# Revit family: KS ALU-PU 80 -s-, DS 50, M10-M12, Ø 88,9-168,3
name_source: partatom
category: HLS-Bauteile
revit_build: Autodesk Revit 2017 (Build: 20190507_1515(x64)
units: mm (PartAtom-declared; Revit-internal decimal feet)

## family parameters
Arbeitsebenenbasiert = Ja
Beim Laden mit Abzugskörper schneiden = Nein
Bemaßung runder Anschluss = Durchmesser verwenden
Gemeinsam genutzt = Ja
Immer vertikal = Nein
Raumberechnungspunkt = Nein
Teiletyp = Normal

## types (7) — shared parameters
Anschluss = M10/M12
Baustoffklasse = B2
DS = 50 mm  [stored 0.164042 ft]
DVS = 18 mm  [stored 0.0590551 ft]
Dichte Kern = 80 kg/m³
Dichte Mantel = 2.700 kg/m³
Dicke Mantel = 0,08 mm
Dämmkörper = ALU/PU
Dämmstärke = 50 mm  [stored 0.164042 ft]
Fabrikat = MEFA
Firma = MEFA Befestigungs- und Montagesysteme GmbH
HGA = 22 mm  [stored 0.0721785 ft]
Kurztext1 = Kälteschelle RG80s ALU/PU
Material = Stahl
Material Mantel = Alufolie
Materialname = S235
Mengeneinheit = St
Oberflaeche = galvanisch verzinkt
Rohrschellentyp = Maxima PSM
Vorgabe-Ansicht = 1219 mm
Wasserdampfdiffusionswiderstand = 18750 µ
Wärmeleitfähigkeit = 0.025 W/mK
max. Temperaturbeständigkeit = 120 °C
mittl. Nenndruckfestigkeit Kern = 0,5 N/mm²
stat. Belastung Kern = 0,1 N/mm²
vpe = 1 St

## per-type parameters (varying)
- Kälteschelle ALU-PU 80 -s-, DS 50, M10/M12, Ø 88,9: A=75 mm; AB=1 mm  [stored 0.00328084 ft]; Anschlußhöhe=75 mm; Artikelnummer=75508942; B=266 mm; Breite=252 mm; D=89 mm; D0=189 mm; DF1=35 mm  [stored 0.114829 ft]; DF2=35 mm  [stored 0.114829 ft]; Dmax=90 mm  [stored 0.295276 ft]; Dmin=88 mm  [stored 0.288714 ft]; EAN=4250928443267; Gewicht=0.77 kg; Gewicht pro Bauteil=0.77 kg; H=217 mm; Kurztext2=88,9 mm Iso 50 x 83 mm M10/M12; L=83 mm  [stored 0.27231 ft]; MB=30 mm  [stored 0.0984252 ft]; MD=3 mm  [stored 0.00984252 ft]; R=94 mm; RM=97 mm; Rohraußendurchmesser Stahl=88,9 mm; S=231 mm; Schalenlänge=83 mm; max. zul. Last=0.80 kN
- Kälteschelle ALU-PU 80 -s-, DS 50, M10/M12, Ø108: A=75 mm; AB=2 mm  [stored 0.00656168 ft]; Anschlußhöhe=76 mm; Artikelnummer=75510842; B=288 mm; Breite=272 mm; D=108 mm  [stored 0.354331 ft]; D0=208 mm; DF1=36 mm  [stored 0.11811 ft]; DF2=36 mm  [stored 0.11811 ft]; Dmax=110 mm  [stored 0.360892 ft]; Dmin=106 mm  [stored 0.347769 ft]; EAN=4250928443281; Gewicht=0.85 kg; Gewicht pro Bauteil=0.85 kg; H=236 mm; Kurztext2=108 mm Iso 50 x 83 mm M10/M12; L=83 mm  [stored 0.27231 ft]; MB=30 mm  [stored 0.0984252 ft]; MD=3 mm  [stored 0.00984252 ft]; R=104 mm; RM=107 mm  [stored 0.35105 ft]; Rohraußendurchmesser Stahl=108 mm; S=252 mm; Schalenlänge=83 mm; max. zul. Last=0.90 kN
- Kälteschelle ALU-PU 80 -s-, DS 50, M10/M12, Ø114,3: A=75 mm; AB=0 mm  [stored 0 ft]; Anschlußhöhe=77 mm; Artikelnummer=75511442; B=298 mm; Breite=290 mm; D=114 mm  [stored 0.374016 ft]; D0=214 mm; DF1=38 mm  [stored 0.124672 ft]; DF2=38 mm  [stored 0.124672 ft]; Dmax=116 mm  [stored 0.380577 ft]; Dmin=114 mm  [stored 0.374016 ft]; EAN=4250928443304; Gewicht=0.88 kg; Gewicht pro Bauteil=0.88 kg; H=242 mm; Kurztext2=114,3 mm Iso 50 x 83 mm M10/M12; L=83 mm  [stored 0.27231 ft]; MB=30 mm  [stored 0.0984252 ft]; MD=3 mm  [stored 0.00984252 ft]; R=107 mm  [stored 0.35105 ft]; RM=110 mm  [stored 0.360892 ft]; Rohraußendurchmesser Stahl=114,3 mm; S=260 mm; Schalenlänge=83 mm; max. zul. Last=1.00 kN
- Kälteschelle ALU-PU 80 -s-, DS 50, M10/M12, Ø133: A=76 mm  [stored 0.249344 ft]; AB=1 mm  [stored 0.00328084 ft]; Anschlußhöhe=75 mm; Artikelnummer=76513344; B=308 mm; Breite=308 mm; D=133 mm  [stored 0.436352 ft]; D0=233 mm; DF1=32 mm  [stored 0.104987 ft]; DF2=32 mm  [stored 0.104987 ft]; Dmax=136 mm; Dmin=132 mm  [stored 0.433071 ft]; EAN=4250928445254; Gewicht=1.29 kg; Gewicht pro Bauteil=1.29 kg; H=263 mm; Kurztext2=133 mm Iso 50 x 100 mm M10/M12; L=100 mm  [stored 0.328084 ft]; MB=35 mm  [stored 0.114829 ft]; MD=4 mm  [stored 0.0131234 ft]; R=117 mm; RM=121 mm; Rohraußendurchmesser Stahl=133 mm; S=276 mm; Schalenlänge=100 mm; max. zul. Last=1.20 kN
- Kälteschelle ALU-PU 80 -s-, DS 50, M10/M12, Ø139,7: A=76 mm  [stored 0.249344 ft]; AB=2 mm  [stored 0.00656168 ft]; Anschlußhöhe=75 mm; Artikelnummer=76514044; B=315 mm; Breite=323 mm; D=140 mm; D0=240 mm; DF1=33 mm  [stored 0.108268 ft]; DF2=32 mm  [stored 0.104987 ft]; Dmax=142 mm; Dmin=138 mm  [stored 0.452756 ft]; EAN=4250928445285; Gewicht=1.32 kg; Gewicht pro Bauteil=1.32 kg; H=270 mm; Kurztext2=139,7 mm Iso 50 x 100 mm M10/M12; L=100 mm  [stored 0.328084 ft]; MB=35 mm  [stored 0.114829 ft]; MD=4 mm  [stored 0.0131234 ft]; R=120 mm; RM=124 mm; Rohraußendurchmesser Stahl=139,7 mm; S=282 mm; Schalenlänge=100 mm; max. zul. Last=1.20 kN
- Kälteschelle ALU-PU 80 -s-, DS 50, M10-M12, Ø159: A=76 mm  [stored 0.249344 ft]; AB=1 mm  [stored 0.00328084 ft]; Anschlußhöhe=77 mm; Artikelnummer=76515944; B=340 mm; Breite=332 mm; D=159 mm; D0=259 mm; DF1=35 mm  [stored 0.114829 ft]; DF2=35 mm  [stored 0.114829 ft]; Dmax=162 mm; Dmin=158 mm; EAN=4250928445315; Gewicht=1.45 kg; Gewicht pro Bauteil=1.45 kg; H=289 mm; Kurztext2=159 mm Iso 50 x 100 mm M10/M12; L=100 mm  [stored 0.328084 ft]; MB=35 mm  [stored 0.114829 ft]; MD=4 mm  [stored 0.0131234 ft]; R=130 mm; RM=134 mm; Rohraußendurchmesser Stahl=159 mm; S=305 mm; Schalenlänge=100 mm; max. zul. Last=1.30 kN
- Kälteschelle ALU-PU 80 -s-, DS 50, M10/M12, Ø168,3: A=76 mm  [stored 0.249344 ft]; AB=2 mm  [stored 0.00656168 ft]; Anschlußhöhe=76 mm; Artikelnummer=76516844; B=344 mm; Breite=342 mm; D=168 mm; D0=268 mm; DF1=33 mm  [stored 0.108268 ft]; DF2=33 mm  [stored 0.108268 ft]; Dmax=170 mm; Dmin=166 mm; EAN=4250928445346; Gewicht=1.48 kg; Gewicht pro Bauteil=1.48 kg; H=298 mm; Kurztext2=168,3 mm Iso 50 x 100 mm M10/M12; L=100 mm  [stored 0.328084 ft]; MB=35 mm  [stored 0.114829 ft]; MD=4 mm  [stored 0.0131234 ft]; R=134 mm; RM=138 mm  [stored 0.452756 ft]; Rohraußendurchmesser Stahl=168,3 mm; S=311 mm; Schalenlänge=100 mm; max. zul. Last=1.40 kN

note: [stored X ft] marks values corroborated as IEEE doubles in the binary element streams (Revit-internal decimal feet)

## geometry (parser evidence)
native form markers: Sweep x6
no freeform markers — native parametric forms only
